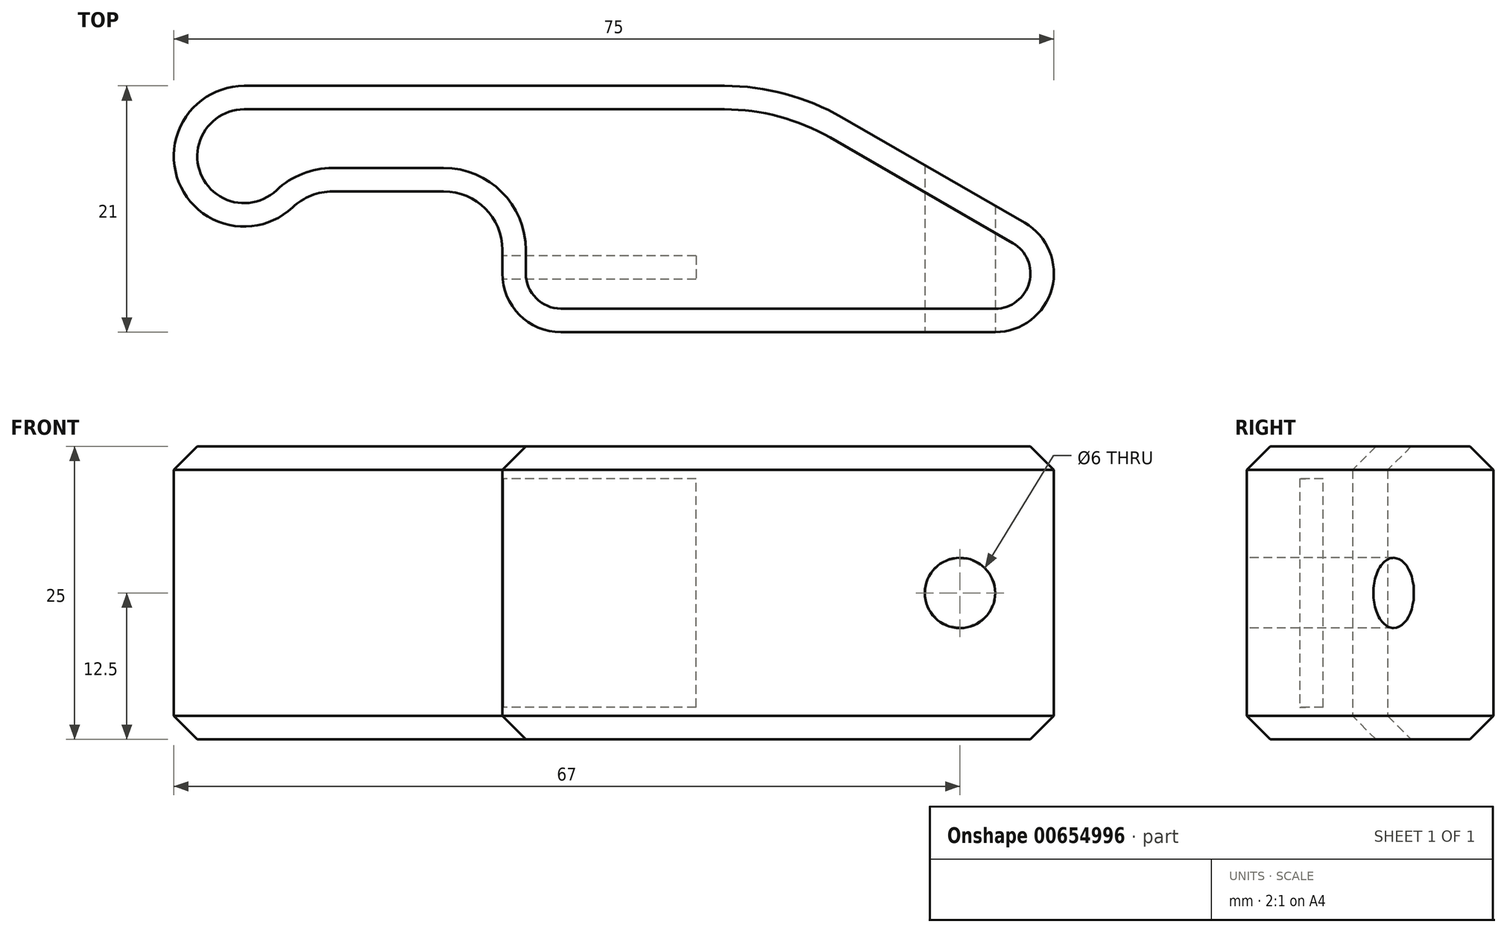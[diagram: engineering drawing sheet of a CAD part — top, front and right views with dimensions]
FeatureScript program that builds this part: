
annotation { "Feature Type Name" : "Feature", "Feature Type Description" : "" }
export const myFeature = defineFeature(function(context is Context, id is Id, definition is map)
    precondition{}
    {
        {
            var Q0;
            Q0=qCreatedBy(makeId("Top.planeOp"),FACE);
            var sketch = newSketch(context, id + "F0", { "sketchPlane" : qUnion([Q0])});
            skLineSegment(sketch, "E0", {"start": v(33.93, 11.32) * mm, "end": v(49.5, 2.33) * mm});
            skLineSegment(sketch, "E1", {"start": v(47, -7) * mm, "end": v(10, -7) * mm});
            skLineSegment(sketch, "E2", {"start": v(5, -2) * mm, "end": v(5, 0) * mm});
            skPoint(sketch, "E3.visualSharp", {"position": v(0, 0) * mm});
            skArc(sketch, "E3.filletArc", {"start": v(5, 0) * mm, "mid": v(3.54, 3.54) * mm, "end": v(0, 5) * mm});
            skPoint(sketch, "E4.visualSharp", {"position": v(33.93, 11.32) * mm});
            skArc(sketch, "E4.filletArc", {"start": v(33.93, 11.32) * mm, "mid": v(29.1, 13.32) * mm, "end": v(23.93, 14) * mm});
            skArc(sketch, "E5.filletArc", {"start": v(47, -7) * mm, "mid": v(51.83, -3.3) * mm, "end": v(49.5, 2.33) * mm});
            skPoint(sketch, "E6.visualSharp", {"position": v(5, -7) * mm});
            skArc(sketch, "E6.filletArc", {"start": v(5, -2) * mm, "mid": v(6.46, -5.54) * mm, "end": v(10, -7) * mm});
            skLineSegment(sketch, "E7", {"start": v(23.93, 14) * mm, "end": v(-17, 14) * mm});
            skLineSegment(sketch, "E8", {"start": v(0, 5) * mm, "end": v(-9.45, 5) * mm});
            skArc(sketch, "E9", {"start": v(-17, 14) * mm, "mid": v(-22.58, 5.78) * mm, "end": v(-12.88, 3.64) * mm});
            skPoint(sketch, "E10.visualSharp", {"position": v(-11.8, 5) * mm});
            skArc(sketch, "E10.filletArc", {"start": v(-9.45, 5) * mm, "mid": v(-11.3, 4.65) * mm, "end": v(-12.88, 3.64) * mm});
            skLineSegment(sketch, "E11", {"start": v(-23, -19.5) * mm, "end": v(-23, 8) * mm, "construction": true});
            skLineSegment(sketch, "E12", {"start": v(52, -19.5) * mm, "end": v(52, -2) * mm, "construction": true});
            skSolve(sketch);
        }
        {
            var Q0;
            Q0 = qSketchRegion(id + "F0", true);
            extrude(context, id + "F1", {"entities" : qUnion([Q0]), "endBound" : BoundingType.SYMMETRIC, "depth" : 25 * mm, "offsetDistance" : 25 * mm});
        }
        {
            var Q0;
            Q0=makeQuery(id+"F1.opExtrude","SWEPT_FACE",FACE,{"disambiguationData":[OSD([sQuery(id+"F0.wireOp",EDGE,"E2")])]});
            var sketch = newSketch(context, id + "F2", { "sketchPlane" : qUnion([Q0])});
            skLineSegment(sketch, "E13.bottom", {"start": v(0.5, -9.75) * mm, "end": v(2.5, -9.75) * mm});
            skLineSegment(sketch, "E13.top", {"start": v(0.5, 9.75) * mm, "end": v(2.5, 9.75) * mm});
            skLineSegment(sketch, "E13.left", {"start": v(0.5, -9.75) * mm, "end": v(0.5, 9.75) * mm});
            skLineSegment(sketch, "E13.right", {"start": v(2.5, -9.75) * mm, "end": v(2.5, 9.75) * mm});
            skLineSegment(sketch, "E14", {"start": v(2.5, 12.5) * mm, "end": v(2.5, -12.5) * mm, "construction": true});
            skPoint(sketch, "E15", {"position": v(2.5, 0) * mm});
            skPoint(sketch, "E15.positionSnap0", {"position": v(2.5, 0) * mm});
            skSolve(sketch);
        }
        {
            var Q0;
            Q0 = qSketchRegion(id + "F2", true);
            extrude(context, id + "F3", {"entities" : qUnion([Q0]), "operationType" : NewBodyOperationType.REMOVE, "oppositeDirection" : true, "depth" : 16.5 * mm, "offsetDistance" : 25 * mm});
        }
        {
            var Q0;
            Q0=makeQuery(id+"F1.opExtrude","CAP_FACE",FACE,{"disambiguationData":[OSD([sQuery(id+"F0.wireOp",EDGE,"E0"),sQuery(id+"F0.wireOp",EDGE,"E1"),sQuery(id+"F0.wireOp",EDGE,"E2"),sQuery(id+"F0.wireOp",EDGE,"E3.filletArc"),sQuery(id+"F0.wireOp",EDGE,"E4.filletArc"),sQuery(id+"F0.wireOp",EDGE,"E5.filletArc"),sQuery(id+"F0.wireOp",EDGE,"E6.filletArc"),sQuery(id+"F0.wireOp",EDGE,"E7"),sQuery(id+"F0.wireOp",EDGE,"E8"),sQuery(id+"F0.wireOp",EDGE,"E9"),sQuery(id+"F0.wireOp",EDGE,"E10.filletArc")])],"isStart":false});
            var Q1;
            Q1=makeQuery(id+"F1.opExtrude","CAP_FACE",FACE,{"disambiguationData":[OSD([sQuery(id+"F0.wireOp",EDGE,"E0"),sQuery(id+"F0.wireOp",EDGE,"E1"),sQuery(id+"F0.wireOp",EDGE,"E2"),sQuery(id+"F0.wireOp",EDGE,"E3.filletArc"),sQuery(id+"F0.wireOp",EDGE,"E4.filletArc"),sQuery(id+"F0.wireOp",EDGE,"E5.filletArc"),sQuery(id+"F0.wireOp",EDGE,"E6.filletArc"),sQuery(id+"F0.wireOp",EDGE,"E7"),sQuery(id+"F0.wireOp",EDGE,"E8"),sQuery(id+"F0.wireOp",EDGE,"E9"),sQuery(id+"F0.wireOp",EDGE,"E10.filletArc")])],"isStart":true});
            chamfer(context, id + "F4", {"entities" : qUnion([Q0, Q1]), "width" : 2 * mm, "tangentPropagation" : true});
        }
        {
            var Q0;
            Q0=makeQuery(id+"F1.opExtrude","SWEPT_FACE",FACE,{"disambiguationData":[OSD([sQuery(id+"F0.wireOp",EDGE,"E1")])]});
            var sketch = newSketch(context, id + "F5", { "sketchPlane" : qUnion([Q0])});
            skLineSegment(sketch, "E16", {"start": v(44, 10.5) * mm, "end": v(44, -10.5) * mm, "construction": true});
            skCircle(sketch, "E17", {"center": v(44, 0) * mm, "radius": 3 * mm});
            skSolve(sketch);
        }
        {
            var Q0;
            Q0 = qSketchRegion(id + "F5", true);
            extrude(context, id + "F6", {"entities" : qUnion([Q0]), "operationType" : NewBodyOperationType.REMOVE, "endBound" : BoundingType.THROUGH_ALL, "oppositeDirection" : true, "depth" : 25 * mm, "offsetDistance" : 25 * mm});
        }
    });
